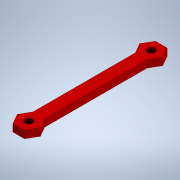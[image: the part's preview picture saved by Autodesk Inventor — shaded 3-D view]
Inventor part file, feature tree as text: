
AUTODESK INVENTOR PART (.ipt)
format: ipt  version: 2020 (Build 240168000, 168)  size: 122,880 bytes
history: native  units: in
note: dims shown in document units (in); Inventor stores cm internally (conversion verified against a paired STEP export)
features: extrude x1, sketch x1
ambient origin geometry x8: Origin, YZ Plane, XZ Plane, XY Plane, X Axis, Y Axis, Z Axis, Center Point
bodies: Solid1 (feature_tree)
feature tree (2):
  extrude  "Extrusion1"  Depth=0.315in
  sketch  "Sketch1"  dims[d1=1.6142in d2=0.315in d3=0.122in d4=0.122in d5=0.1181in d6=0.0in]
